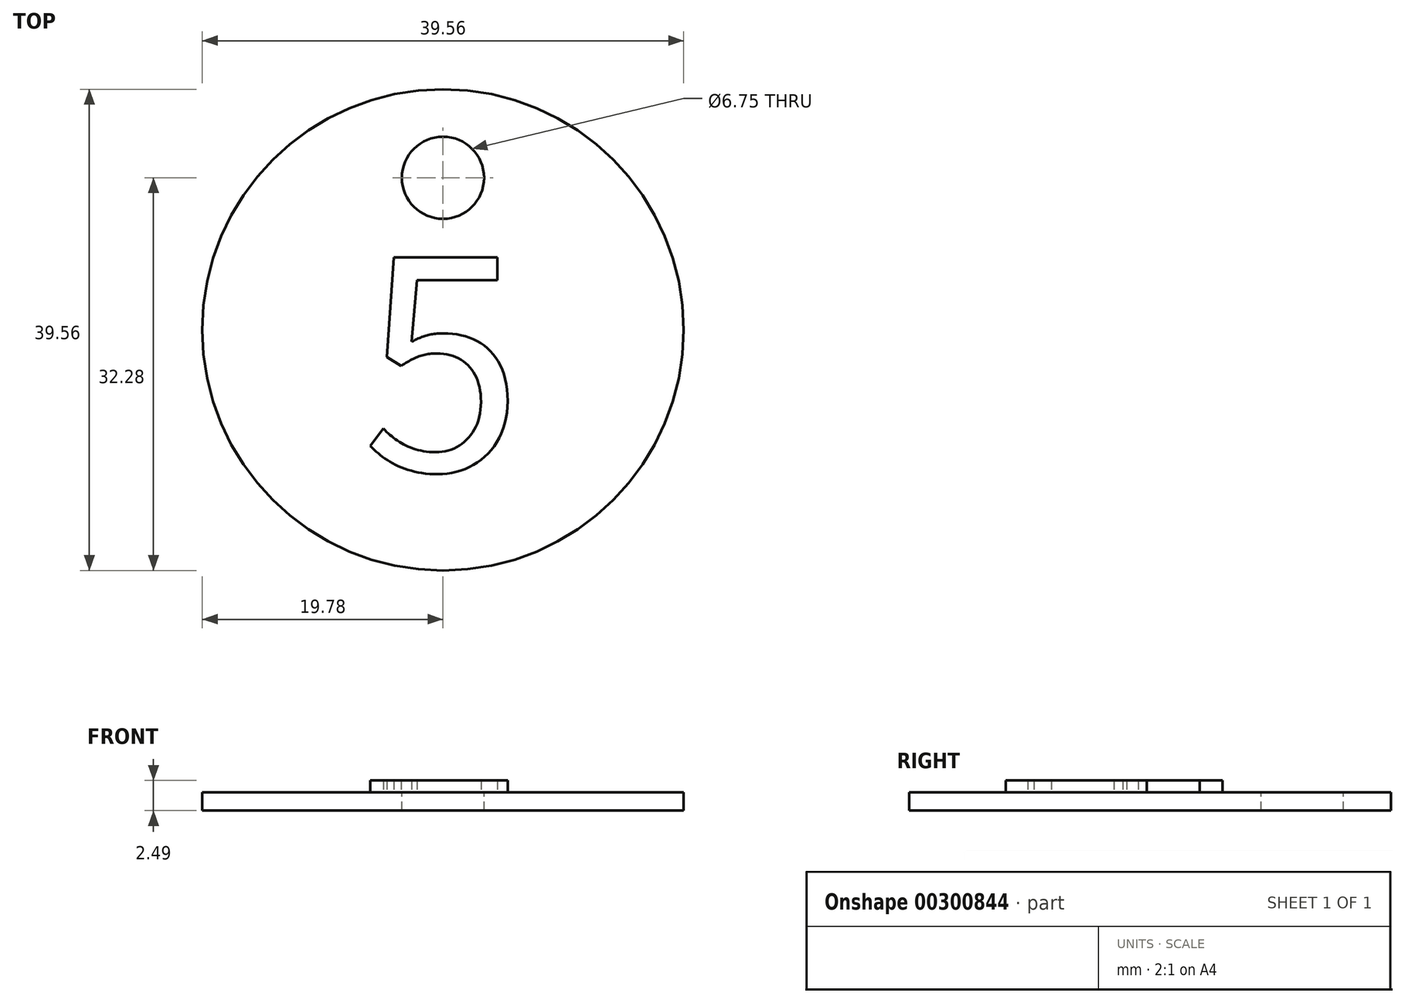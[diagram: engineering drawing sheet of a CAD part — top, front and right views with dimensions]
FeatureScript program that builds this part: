
annotation { "Feature Type Name" : "Feature", "Feature Type Description" : "" }
export const myFeature = defineFeature(function(context is Context, id is Id, definition is map)
    precondition{}
    {
        {
            var Q0;
            Q0=qCreatedBy(makeId("Top.planeOp"),FACE);
            var sketch = newSketch(context, id + "F0", { "sketchPlane" : qUnion([Q0])});
            skCircle(sketch, "E0", {"center": v(0, 0) * mm, "radius": 19.78 * mm});
            skSolve(sketch);
        }
        {
            var Q0;
            Q0 = qSketchRegion(id + "F0", true);
            extrude(context, id + "F1", {"entities" : qUnion([Q0]), "depth" : 1.49 * mm});
        }
        {
            var Q0;
            Q0=makeQuery(id+"F1.opExtrude","CAP_FACE",FACE,{"disambiguationData":[OSD([sQuery(id+"F0.wireOp",EDGE,"E0")])],"isStart":false});
            var sketch = newSketch(context, id + "F2", { "sketchPlane" : qUnion([Q0])});
            skCircle(sketch, "E1", {"center": v(0, 12.5) * mm, "radius": 3.38 * mm});
            skSolve(sketch);
        }
        {
            var Q0;
            Q0 = qSketchRegion(id + "F2", true);
            extrude(context, id + "F3", {"entities" : qUnion([Q0]), "operationType" : NewBodyOperationType.REMOVE, "oppositeDirection" : true, "depth" : 25 * mm});
        }
        {
            var Q0;
            Q0=makeQuery(id+"F1.opExtrude","CAP_FACE",FACE,{"disambiguationData":[OSD([sQuery(id+"F0.wireOp",EDGE,"E0")])],"isStart":false});
            var sketch = newSketch(context, id + "F4", { "sketchPlane" : qUnion([Q0])});
            skText(sketch, "E2", { "text": "5", "fontName": "NotoSansCJKjp-Regular.otf"});
            const initialGuessF4  = {"E2": [-0.00665, -0.01156, 1, 0, 0.0172]};
            skSetInitialGuess(sketch, initialGuessF4);
            skSolve(sketch);
        }
        {
            var Q0;
            Q0 = qSketchRegion(id + "F4", true);
            extrude(context, id + "F5", {"entities" : qUnion([Q0]), "operationType" : NewBodyOperationType.ADD, "depth" : 1 * mm});
        }
    });
